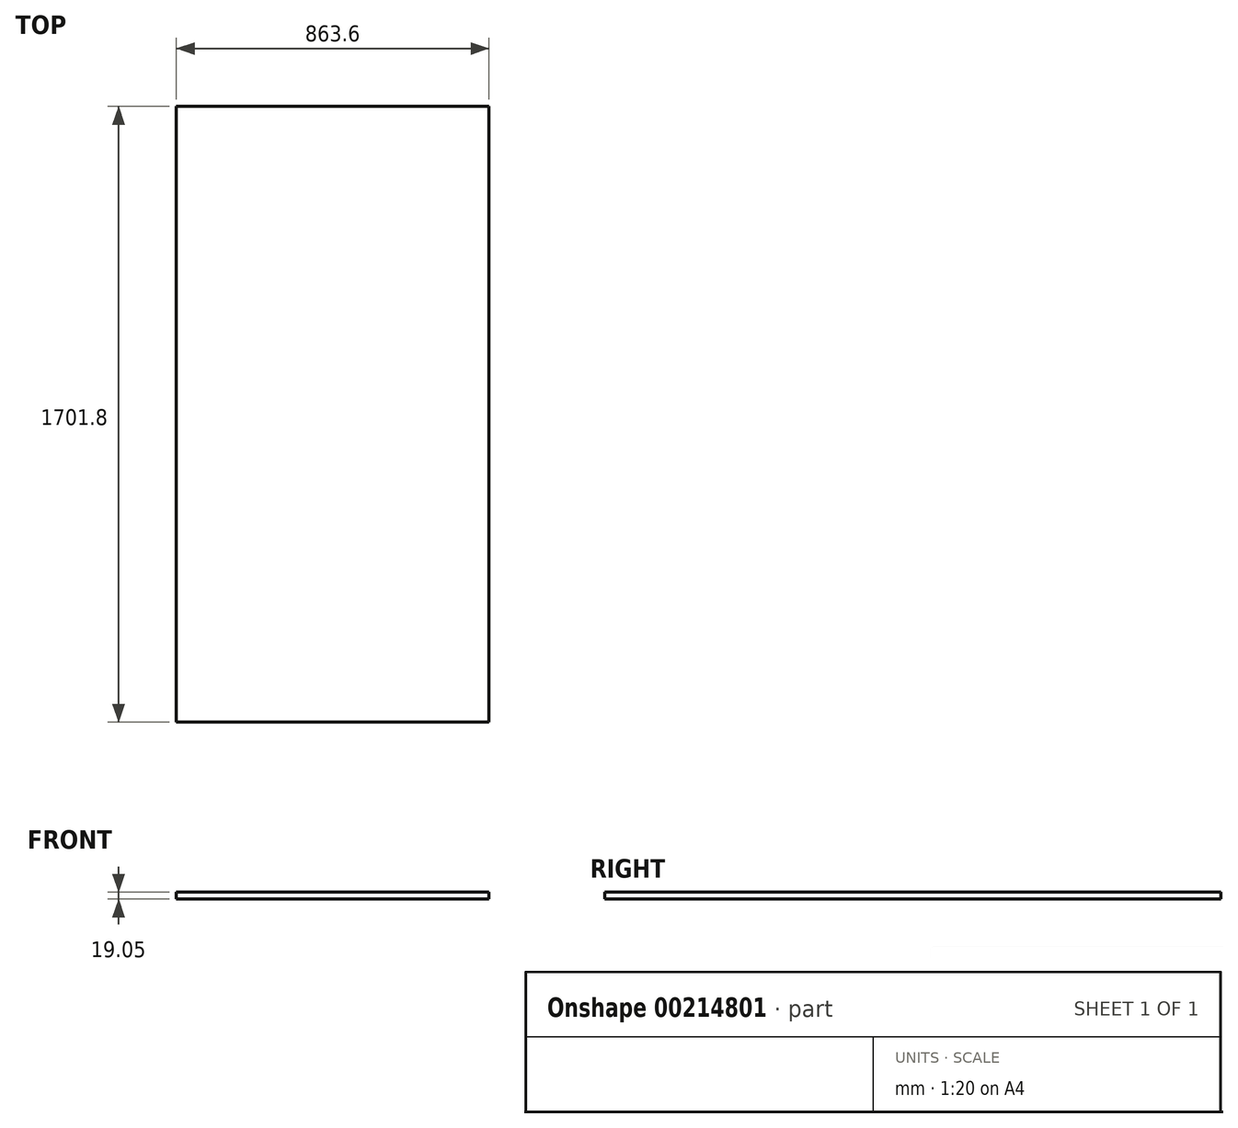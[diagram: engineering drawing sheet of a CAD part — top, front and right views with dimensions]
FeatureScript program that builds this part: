
annotation { "Feature Type Name" : "Feature", "Feature Type Description" : "" }
export const myFeature = defineFeature(function(context is Context, id is Id, definition is map)
    precondition{}
    {
        {
            var Q0;
            Q0=qCreatedBy(makeId("Top.planeOp"),FACE);
            var sketch = newSketch(context, id + "F0", { "sketchPlane" : qUnion([Q0])});
            skLineSegment(sketch, "E0.bottom", {"start": v(0, 0) * mm, "end": v(863.6, 0) * mm});
            skLineSegment(sketch, "E0.top", {"start": v(0, -1701.8) * mm, "end": v(863.6, -1701.8) * mm});
            skLineSegment(sketch, "E0.left", {"start": v(0, 0) * mm, "end": v(0, -1701.8) * mm});
            skLineSegment(sketch, "E0.right", {"start": v(863.6, 0) * mm, "end": v(863.6, -1701.8) * mm});
            skSolve(sketch);
        }
        {
            var Q0;
            Q0=makeQuery(id+"F0.imprint","IMPRINT",FACE,{"disambiguationData":[TD([[makeQuery(id+"F0.imprint","IMPRINT",EDGE,{"derivedFrom":sQuery(id+"F0.wireOp",EDGE,"E0.bottom")}),-1.0]])]});
            extrude(context, id + "F1", {"entities" : qUnion([Q0]), "depth" : 19.05 * mm});
        }
    });
